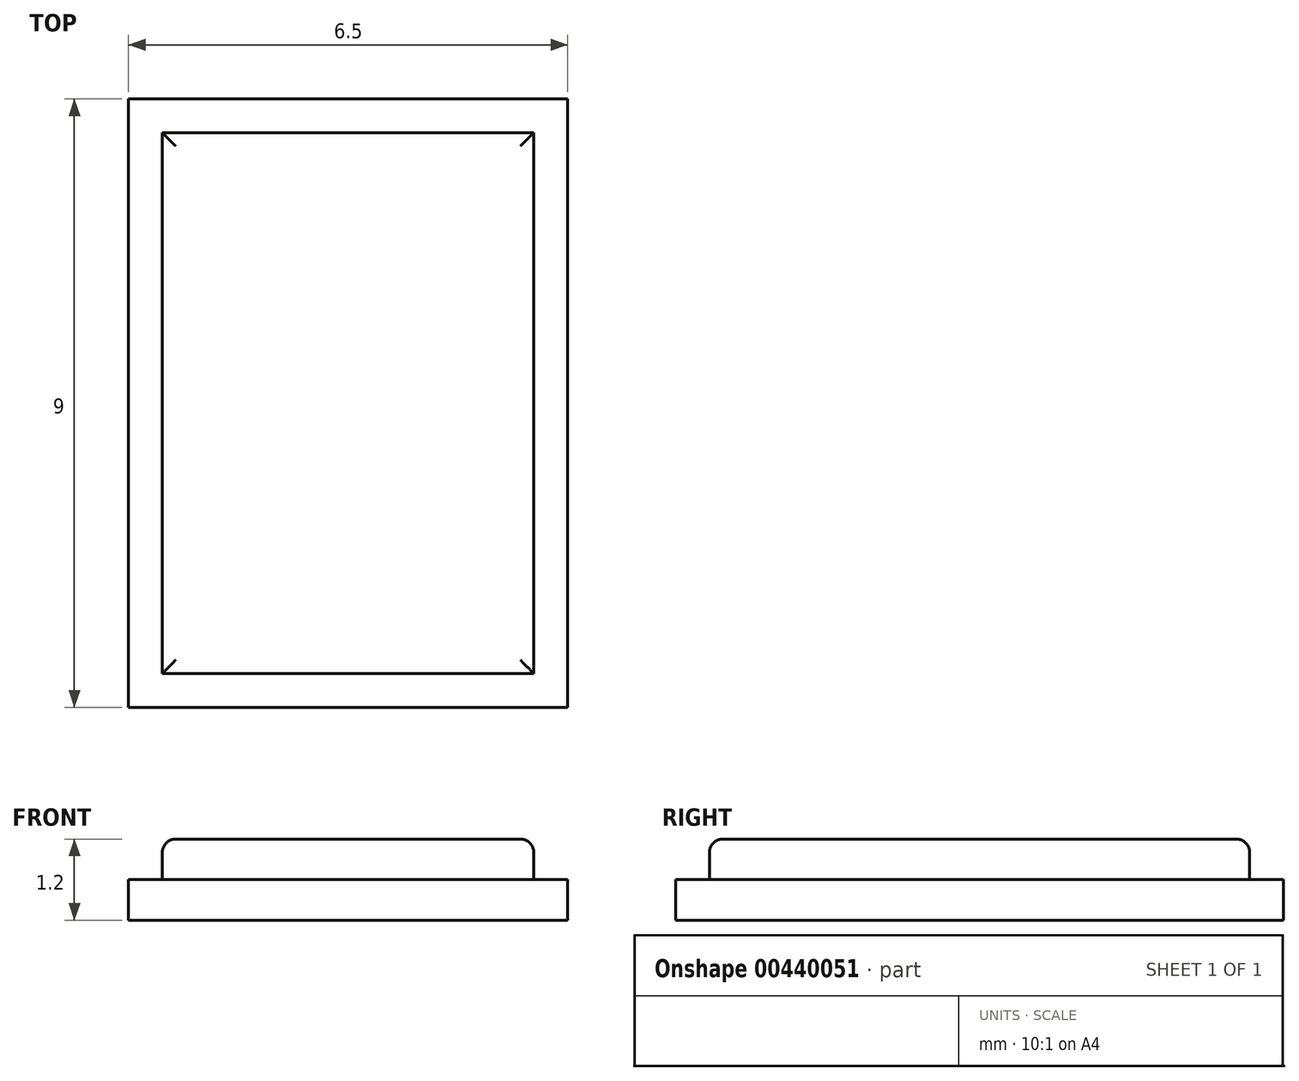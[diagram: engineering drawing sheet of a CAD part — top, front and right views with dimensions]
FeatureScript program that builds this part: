
annotation { "Feature Type Name" : "Feature", "Feature Type Description" : "" }
export const myFeature = defineFeature(function(context is Context, id is Id, definition is map)
    precondition{}
    {
        {
            var Q0;
            Q0=qCreatedBy(makeId("Top.planeOp"),FACE);
            var sketch = newSketch(context, id + "F0", { "sketchPlane" : qUnion([Q0])});
            skLineSegment(sketch, "E0.bottom", {"start": v(0, 0) * mm, "end": v(6.5, 0) * mm});
            skLineSegment(sketch, "E0.top", {"start": v(0, 9) * mm, "end": v(6.5, 9) * mm});
            skLineSegment(sketch, "E0.left", {"start": v(0, 0) * mm, "end": v(0, 9) * mm});
            skLineSegment(sketch, "E0.right", {"start": v(6.5, 0) * mm, "end": v(6.5, 9) * mm});
            skLineSegment(sketch, "E1", {"start": v(0, 0) * mm, "end": v(0.5, 0) * mm, "construction": true});
            skLineSegment(sketch, "E2", {"start": v(0.5, 0) * mm, "end": v(6, 0) * mm, "construction": true});
            skLineSegment(sketch, "E3", {"start": v(0.5, 0) * mm, "end": v(0.5, 0.5) * mm, "construction": true});
            skLineSegment(sketch, "E4.bottom", {"start": v(0.5, 0.5) * mm, "end": v(6, 0.5) * mm, "construction": true});
            skLineSegment(sketch, "E4.top", {"start": v(0.5, 8.5) * mm, "end": v(6, 8.5) * mm, "construction": true});
            skLineSegment(sketch, "E4.left", {"start": v(0.5, 0.5) * mm, "end": v(0.5, 8.5) * mm, "construction": true});
            skLineSegment(sketch, "E4.right", {"start": v(6, 0.5) * mm, "end": v(6, 8.5) * mm, "construction": true});
            skSolve(sketch);
        }
        {
            var Q0;
            Q0=makeQuery(id+"F0.imprint","IMPRINT",FACE,{"disambiguationData":[TD([[makeQuery(id+"F0.imprint","IMPRINT",EDGE,{"derivedFrom":sQuery(id+"F0.wireOp",EDGE,"E0.bottom")}),1.0]])]});
            var sketch = newSketch(context, id + "F1", { "sketchPlane" : qUnion([Q0])});
            skLineSegment(sketch, "E5.bottom", {"start": v(0, 0) * mm, "end": v(0.5, 0) * mm, "construction": true});
            skLineSegment(sketch, "E5.top", {"start": v(0, 0.5) * mm, "end": v(0.5, 0.5) * mm, "construction": true});
            skLineSegment(sketch, "E5.left", {"start": v(0, 0) * mm, "end": v(0, 0.5) * mm, "construction": true});
            skLineSegment(sketch, "E5.right", {"start": v(0.5, 0) * mm, "end": v(0.5, 0.5) * mm, "construction": true});
            skLineSegment(sketch, "E6.bottom", {"start": v(0.5, 0.5) * mm, "end": v(6, 0.5) * mm});
            skLineSegment(sketch, "E6.top", {"start": v(0.5, 8.5) * mm, "end": v(6, 8.5) * mm});
            skLineSegment(sketch, "E6.left", {"start": v(0.5, 0.5) * mm, "end": v(0.5, 8.5) * mm});
            skLineSegment(sketch, "E6.right", {"start": v(6, 0.5) * mm, "end": v(6, 8.5) * mm});
            skSolve(sketch);
        }
        {
            var Q0;
            Q0 = qSketchRegion(id + "F0", true);
            extrude(context, id + "F2", {"entities" : qUnion([Q0]), "oppositeDirection" : true, "depth" : .6 * mm});
        }
        {
            var Q0;
            Q0 = qSketchRegion(id + "F1", true);
            extrude(context, id + "F3", {"entities" : qUnion([Q0]), "operationType" : NewBodyOperationType.ADD, "depth" : .6 * mm});
        }
        {
            var Q0;
            Q0=makeQuery(id+"F3.opExtrude","CAP_EDGE",EDGE,{"disambiguationData":[OSD([sQuery(id+"F1.wireOp",EDGE,"E6.left")])],"isStart":false});
            var Q1;
            Q1=makeQuery(id+"F3.opExtrude","CAP_EDGE",EDGE,{"disambiguationData":[OSD([sQuery(id+"F1.wireOp",EDGE,"E6.bottom")])],"isStart":false});
            var Q2;
            Q2=makeQuery(id+"F3.opExtrude","CAP_EDGE",EDGE,{"disambiguationData":[OSD([sQuery(id+"F1.wireOp",EDGE,"E6.right")])],"isStart":false});
            var Q3;
            Q3=makeQuery(id+"F3.opExtrude","CAP_EDGE",EDGE,{"disambiguationData":[OSD([sQuery(id+"F1.wireOp",EDGE,"E6.top")])],"isStart":false});
            fillet(context, id + "F4", {"entities" : qUnion([Q0, Q1, Q2, Q3]), "radius" : .2 * mm, "tangentPropagation" : true, "allowEdgeOverflow" : false});
        }
    });
